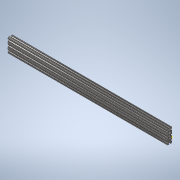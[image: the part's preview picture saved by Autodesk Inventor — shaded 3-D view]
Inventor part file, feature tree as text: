
AUTODESK INVENTOR PART (.ipt)
format: ipt  version: 2020 (Build 240168000, 168)  size: 396,288 bytes
history: native  units: in
note: dims shown in document units (in); Inventor stores cm internally (conversion verified against a paired STEP export)
features: sketch x2, extrude x1
ambient origin geometry x8: Origin, YZ Plane, XZ Plane, XY Plane, X Axis, Y Axis, Z Axis, Center Point
bodies: Solid1 (feature_tree)
feature tree (3):
  extrude  "Extrusion1"  [1 undecoded]
  sketch  "Sketch2"
  sketch  "Sketch1"  dims[d0=34.0in d1=0.0in]
note: 1 required parameter value undecoded (feature->parameter linkage not recoverable at this tier; creation-order binding heuristic only, values carry confidence <= 0.55)
